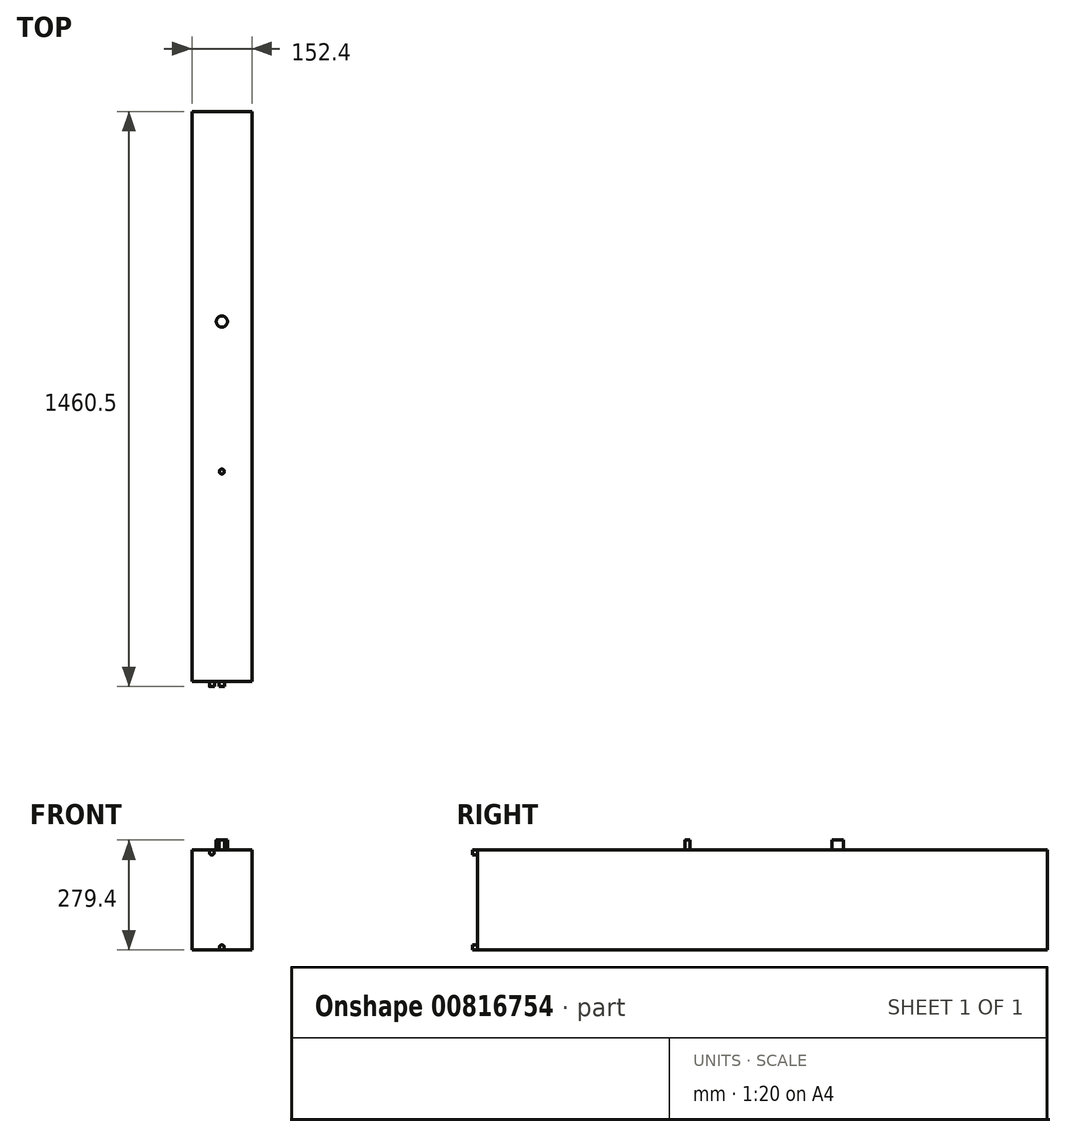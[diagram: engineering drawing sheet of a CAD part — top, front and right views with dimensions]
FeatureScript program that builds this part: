
annotation { "Feature Type Name" : "Feature", "Feature Type Description" : "" }
export const myFeature = defineFeature(function(context is Context, id is Id, definition is map)
    precondition{}
    {
        {
            var Q0;
            Q0=qCreatedBy(makeId("Top.planeOp"),FACE);
            var sketch = newSketch(context, id + "F0", { "sketchPlane" : qUnion([Q0])});
            skLineSegment(sketch, "E0", {"start": v(-38.56, 1396.52) * mm, "end": v(-38.56, -51.28) * mm});
            skLineSegment(sketch, "E1", {"start": v(-38.56, -51.28) * mm, "end": v(113.84, -51.28) * mm});
            skLineSegment(sketch, "E2", {"start": v(113.84, -51.28) * mm, "end": v(113.84, 1396.52) * mm});
            skLineSegment(sketch, "E3", {"start": v(113.84, 1396.52) * mm, "end": v(-38.56, 1396.52) * mm});
            skSolve(sketch);
        }
        {
            var Q0;
            Q0 = qSketchRegion(id + "F0", true);
            extrude(context, id + "F1", {"entities" : qUnion([Q0]), "depth" : 254 * mm, "offsetDistance" : 25.4 * mm});
        }
        {
            var Q0;
            Q0=makeQuery(id+"F1.opExtrude","CAP_FACE",FACE,{"disambiguationData":[OSD([sQuery(id+"F0.wireOp",EDGE,"E0"),sQuery(id+"F0.wireOp",EDGE,"E1"),sQuery(id+"F0.wireOp",EDGE,"E2"),sQuery(id+"F0.wireOp",EDGE,"E3")])],"isStart":false});
            var sketch = newSketch(context, id + "F2", { "sketchPlane" : qUnion([Q0])});
            skPoint(sketch, "E4.centerSnap0", {"position": v(-38.56, 672.62) * mm});
            skPoint(sketch, "E4.centerSnap1", {"position": v(37.64, 1396.52) * mm});
            skPoint(sketch, "E5.centerSnap0", {"position": v(37.64, -51.28) * mm});
            skCircle(sketch, "E6", {"center": v(37.64, 482.12) * mm, "radius": 6.35 * mm});
            skLineSegment(sketch, "E7", {"start": v(37.64, -51.28) * mm, "end": v(37.64, 863.12) * mm});
            skCircle(sketch, "E8", {"center": v(37.64, 863.12) * mm, "radius": 14.29 * mm});
            skSolve(sketch);
        }
        {
            var Q0;
            Q0 = qSketchRegion(id + "F2", true);
            extrude(context, id + "F3", {"entities" : qUnion([Q0]), "operationType" : NewBodyOperationType.ADD, "depth" : 25.4 * mm, "offsetDistance" : 25.4 * mm});
        }
        {
            var Q0;
            Q0=makeQuery(id+"F1.opExtrude","SWEPT_FACE",FACE,{"disambiguationData":[OSD([sQuery(id+"F0.wireOp",EDGE,"E1")])]});
            var sketch = newSketch(context, id + "F4", { "sketchPlane" : qUnion([Q0])});
            skCircle(sketch, "E9", {"center": v(37.64, 6.35) * mm, "radius": 6.35 * mm});
            skPoint(sketch, "E9.centerSnap0", {"position": v(37.64, 0) * mm});
            skLineSegment(sketch, "E10", {"start": v(-38.56, 247.65) * mm, "end": v(12.24, 247.65) * mm});
            skCircle(sketch, "E11", {"center": v(12.24, 247.65) * mm, "radius": 6.35 * mm});
            skSolve(sketch);
        }
        {
            var Q0;
            Q0 = qSketchRegion(id + "F4", true);
            extrude(context, id + "F5", {"entities" : qUnion([Q0]), "operationType" : NewBodyOperationType.ADD, "depth" : 12.7 * mm, "offsetDistance" : 25.4 * mm});
        }
    });
